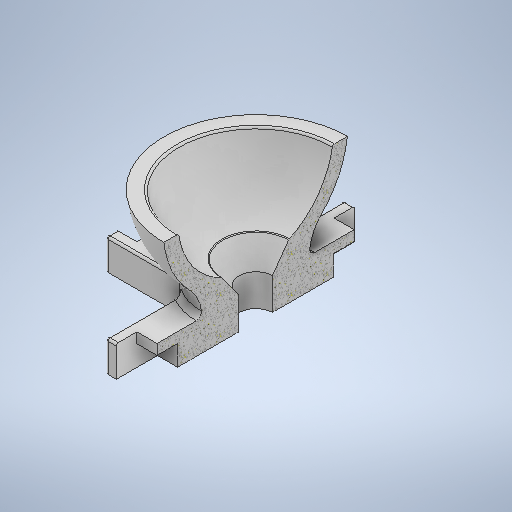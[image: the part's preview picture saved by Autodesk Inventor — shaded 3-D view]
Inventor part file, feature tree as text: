
AUTODESK INVENTOR PART (.ipt)
format: ipt  version: 2025.1 (Build 291241000, 241)  size: 776,192 bytes
history: native  units: mm
features: sketch x9, fillet x8, extrude x7, revolve x2, plane x1, chamfer x1
ambient origin geometry x8: Origin, YZ Plane, XZ Plane, XY Plane, X Axis, Y Axis, Z Axis, Center Point
bodies: Volumenkörper1 (feature_tree)
feature tree (28):
  extrude  "Extrusion1"  Depth=6.0mm TaperAngle=0.0deg
  revolve  "Umdrehung1"
  sketch  "Skizze3"  dims[d7=9.0mm d8=13.2mm]
  fillet  "Rundung1"  [1 undecoded]
  revolve  "Umdrehung2"
  extrude  "Extrusion2"  Depth=9.0mm
  plane  "Arbeitsebene1"
  extrude  "Extrusion3"  Depth=13.2mm
  chamfer  "Fasen1"  [1 undecoded]
  fillet  "Rundung2"  Radius=1.0mm
  fillet  "Rundung3"  Radius=20.0mm
  extrude  "Extrusion4"  TaperAngle=0.0deg  [1 undecoded]
  extrude  "Extrusion5"  Depth=1.0mm
  extrude  "Extrusion6"  Depth=1.0mm TaperAngle=0.0deg
  fillet  "Rundung4"  Radius=2.0mm
  fillet  "Rundung5"  Radius=0.2mm
  fillet  "Rundung6"  Radius=0.2mm
  fillet  "Rundung7"  Radius=6.0mm
  fillet  "Rundung8"  Radius=4.0mm
  extrude  "Extrusion7"  Depth=2.0mm
  sketch  "Skizze1"  dims[d0=10.5mm d1=6.0mm d2=0.0mm d3=0.0mm]
  sketch  "Skizze2"  dims[d5=9.0mm d6=9.0mm]
  sketch  "Skizze4"  dims[d9=90.0deg]
  sketch  "Skizze5"  dims[d10=7.575mm]
  sketch  "Skizze7"  dims[d11=7.575mm]
  sketch  "Skizze8"  dims[d12=7.575mm]
  sketch  "Skizze9"  dims[d13=4.0mm]
  sketch  "Skizze10"  dims[d14=90.0deg d15=0.0mm d16=1.0mm d17=20.0mm d18=0.0mm d19=0.0mm d20=3.3mm d21=20.0mm d22=0.0mm d23=1.7mm d24=2.0mm d25=45.0deg d26=0.2mm d27=0.2mm d28=6.0mm d30=4.0mm d31=0.0mm d32=2.0mm d33=4.0mm d36=4.0mm d37=2.0mm d38=0.0mm d39=2.0mm d40=4.0mm d41=0.0mm d42=0.0mm d43=2.0mm d44=4.0mm d45=4.0mm d46=2.0mm d47=0.0mm d48=4.0mm d49=2.0mm d50=0.0mm d51=2.0mm d52=4.0mm d53=0.0mm d54=3.0mm d55=0.0mm d56=0.5mm d57=0.2mm d58=0.2mm d59=0.2mm d60=0.2mm d61=11.6mm d62=1.0mm d63=30.0mm d64=0.0mm]
note: 3 required parameter values undecoded (feature->parameter linkage not recoverable at this tier; creation-order binding heuristic only, values carry confidence <= 0.55)
